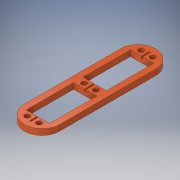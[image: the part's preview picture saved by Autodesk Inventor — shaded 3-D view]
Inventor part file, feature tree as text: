
AUTODESK INVENTOR PART (.ipt)
format: ipt  version: 2017 (Build 210142000, 142)  size: 177,152 bytes
history: native  units: mm
features: extrude x4, sketch x3, fillet x2
ambient origin geometry x8: Origin, YZ Plane, XZ Plane, XY Plane, X Axis, Y Axis, Z Axis, Center Point
bodies: Solid1 (feature_tree)
feature tree (9):
  extrude  "Extrusion1"  Depth=30.0mm
  extrude  "Extrusion2"  TaperAngle=0.0deg  [1 undecoded]
  extrude  "Extrusion4"  Depth=20.0mm
  extrude  "Extrusion5"  Depth=40.5mm
  fillet  "Fillet1"  Radius=11.5mm
  fillet  "Fillet2"  Radius=5.0mm
  sketch  "Sketch1"  dims[d0=30.0mm d1=112.0mm]
  sketch  "Sketch2"  dims[d2=5.0mm d3=0.0mm]
  sketch  "Sketch3"  dims[d4=5.0mm d5=20.0mm d6=40.5mm d7=11.5mm d8=5.0mm d9=0.0mm d13=4.0mm d14=4.0mm d15=2.75mm d16=2.75mm d17=4.5mm d18=2.5mm d19=0.0mm d20=6.5mm d21=1.2mm d22=2.0mm d23=0.0mm]
note: 1 required parameter value undecoded (feature->parameter linkage not recoverable at this tier; creation-order binding heuristic only, values carry confidence <= 0.55)
